# Revit family: Cumberland-Lisa-Lounge1
name_source: partatom
category: Furniture
revit_build: Autodesk Revit 2014 (Build: 20130308_1515(x64)
units: mm (PartAtom-declared; Revit-internal decimal feet)

## types (3) — shared parameters
Arms Finish = CUM - Linen - Beige
Assembly Code = E2020200
Back Finish = CUM - Linen - Beige
Bottom Finish = CUM - Linen - Beige
Depth = 26"
Height = 30"
Keynote = 12500
Leg Finish = CUM - UHMW, Black
Low Emitting Finish = Yes
Low Emitting Material = Yes
Manufacturer = Cumberland
Salvage or Reuse = Yes
Seat Dist = 20 1/16"
Seat Finish = CUM - Linen - Beige
Type Comments = Lisa
URL = www.cumberlandfurniture.com
zero-valued in all types: Percentage of Recycled Content

## per-type parameters (varying)
| type | # Seat | Description | Width |
| 2617 | 2 | Lisa 26"W 30"H 26"D | 26" |
| 2618 | 2 | Lisa 46"W 30"H 26"D | 46" |
| 2619 | 3 | Lisa 66"W 30"H 26"D | 66" |

note: column(s) folded — value = type name in every type: Model

## geometry (parser evidence)
native form markers: Sweep x3
no freeform markers — native parametric forms only
